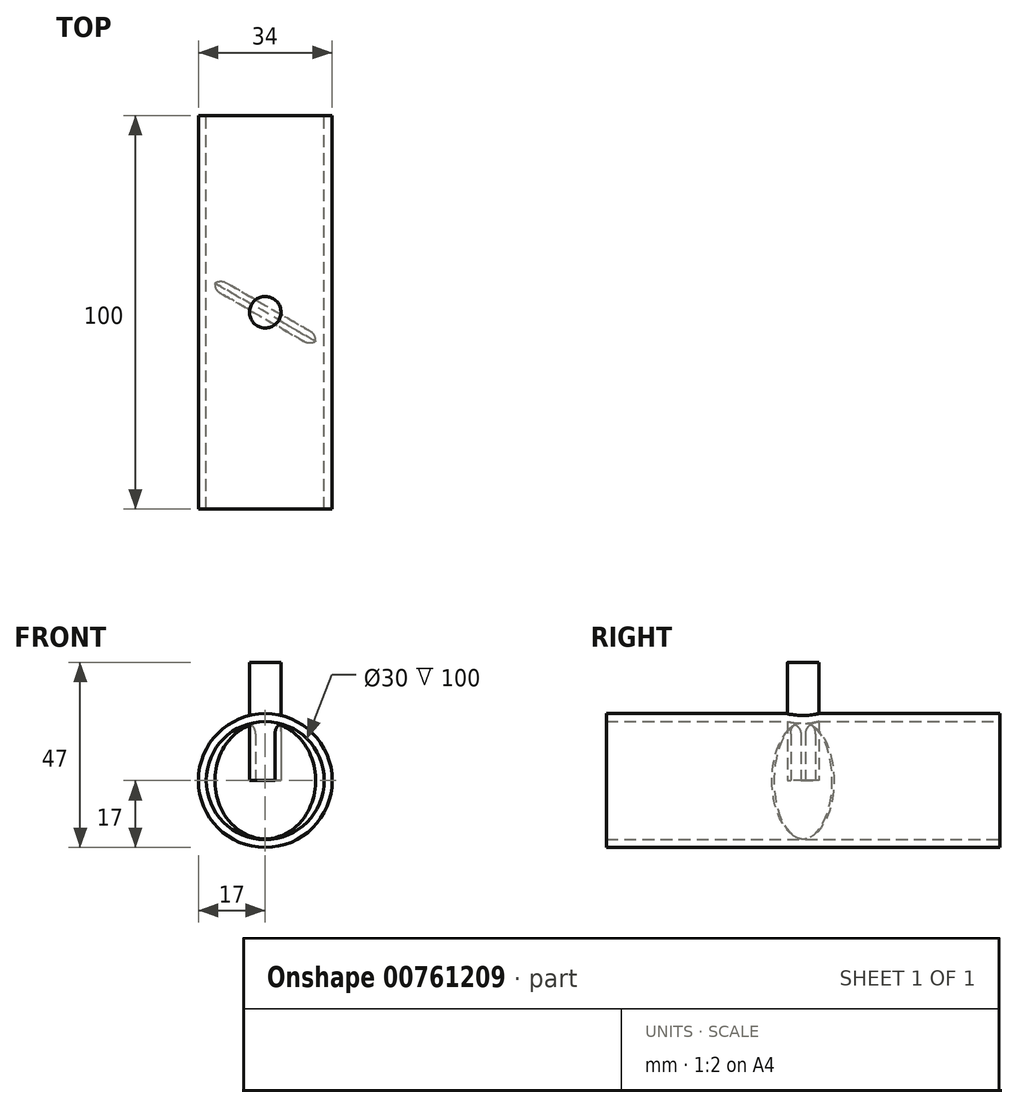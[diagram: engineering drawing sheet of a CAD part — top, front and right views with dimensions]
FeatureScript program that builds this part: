
annotation { "Feature Type Name" : "Feature", "Feature Type Description" : "" }
export const myFeature = defineFeature(function(context is Context, id is Id, definition is map)
    precondition{}
    {
        {
            var Q0;
            Q0=qCreatedBy(makeId("Front.planeOp"),FACE);
            var sketch = newSketch(context, id + "F0", { "sketchPlane" : qUnion([Q0])});
            skCircle(sketch, "E0", {"center": v(0, 0) * mm, "radius": 15 * mm});
            skSolve(sketch);
        }
        {
            var Q0;
            Q0=qCreatedBy(makeId("Top.planeOp"),FACE);
            var sketch = newSketch(context, id + "F1", { "sketchPlane" : qUnion([Q0])});
            skCircle(sketch, "E1", {"center": v(0, 0) * mm, "radius": 4 * mm});
            skSolve(sketch);
        }
        {
            var Q0;
            Q0=qSketchRegion(id+"F1",true);
            extrude(context, id + "F2", {"entities" : qUnion([Q0]), "depth" : 30 * mm, "offsetDistance" : 25.4 * mm});
        }
        {
            var Q0;
            Q0=makeQuery(id+"F0.imprint","IMPRINT",FACE,{"disambiguationData":[TD([[makeQuery(id+"F0.imprint","IMPRINT",EDGE,{"derivedFrom":sQuery(id+"F0.wireOp",EDGE,"E0")}),1.0]])]});
            extrude(context, id + "F3", {"entities" : qUnion([Q0]), "operationType" : NewBodyOperationType.ADD, "endBound" : BoundingType.SYMMETRIC, "depth" : 3 * mm, "offsetDistance" : 25.4 * mm});
        }
        {
            var Q0;
            Q0=makeQuery(id+"F3.boolean.opBoolean","SPLIT",EDGE,{"disambiguationData":[OD(0.0)],"derivedFrom":makeQuery(id+"F3.opExtrude","CAP_EDGE",EDGE,{"disambiguationData":[OSD([sQuery(id+"F0.wireOp",EDGE,"E0")])],"isStart":false})});
            var Q1;
            Q1=makeQuery(id+"F3.boolean.opBoolean","SPLIT",EDGE,{"disambiguationData":[OD(1.0)],"derivedFrom":makeQuery(id+"F3.opExtrude","CAP_EDGE",EDGE,{"disambiguationData":[OSD([sQuery(id+"F0.wireOp",EDGE,"E0")])],"isStart":false})});
            var Q2;
            Q2=makeQuery(id+"F3.boolean.opBoolean","SPLIT",EDGE,{"disambiguationData":[OD(1.0)],"derivedFrom":makeQuery(id+"F3.opExtrude","CAP_EDGE",EDGE,{"disambiguationData":[OSD([sQuery(id+"F0.wireOp",EDGE,"E0")])],"isStart":true})});
            var Q3;
            Q3=makeQuery(id+"F3.boolean.opBoolean","SPLIT",EDGE,{"disambiguationData":[OD(0.0)],"derivedFrom":makeQuery(id+"F3.opExtrude","CAP_EDGE",EDGE,{"disambiguationData":[OSD([sQuery(id+"F0.wireOp",EDGE,"E0")])],"isStart":true})});
            fillet(context, id + "F4", {"entities" : qUnion([Q0, Q1, Q2, Q3]), "radius" : 2.54 * mm, "tangentPropagation" : true, "allowEdgeOverflow" : false});
        }
        {
            var Q0;
            Q0=qCreatedBy(makeId("Front.planeOp"),FACE);
            var sketch = newSketch(context, id + "F5", { "sketchPlane" : qUnion([Q0])});
            skLineSegment(sketch, "E2", {"start": v(0, 76.5) * mm, "end": v(0, -77.52) * mm, "construction": true});
            skSolve(sketch);
        }
        {
            var Q0;
            Q0=makeQuery(id+"F2.opExtrude","SWEPT_BODY",BODY,{"disambiguationData":[OSD([sQuery(id+"F1.wireOp",EDGE,"E1")])]});
            var Q1;
            Q1=sQuery(id+"F5.wireOp",EDGE,"E2");
            transform(context, id + "F6", {"entities" : qUnion([Q0]), "transformType" : TransformType.ROTATION, "transformAxis" : qUnion([Q1]), "angle" : 30 * degree, "makeCopy" : false});
        }
        {
            var Q0;
            Q0=qCreatedBy(makeId("Front.planeOp"),FACE);
            var sketch = newSketch(context, id + "F7", { "sketchPlane" : qUnion([Q0])});
            skCircle(sketch, "E3", {"center": v(0, 0) * mm, "radius": 15 * mm});
            skCircle(sketch, "E4", {"center": v(0, 0) * mm, "radius": 17 * mm});
            skSolve(sketch);
        }
        {
            var Q0;
            Q0=makeQuery(id+"F7.imprint","IMPRINT",FACE,{"disambiguationData":[TD([[makeQuery(id+"F7.imprint","IMPRINT",EDGE,{"derivedFrom":sQuery(id+"F7.wireOp",EDGE,"E3")}),-1.0]])]});
            extrude(context, id + "F8", {"entities" : qUnion([Q0]), "operationType" : NewBodyOperationType.ADD, "endBound" : BoundingType.SYMMETRIC, "depth" : 100 * mm, "offsetDistance" : 25 * mm});
        }
    });
